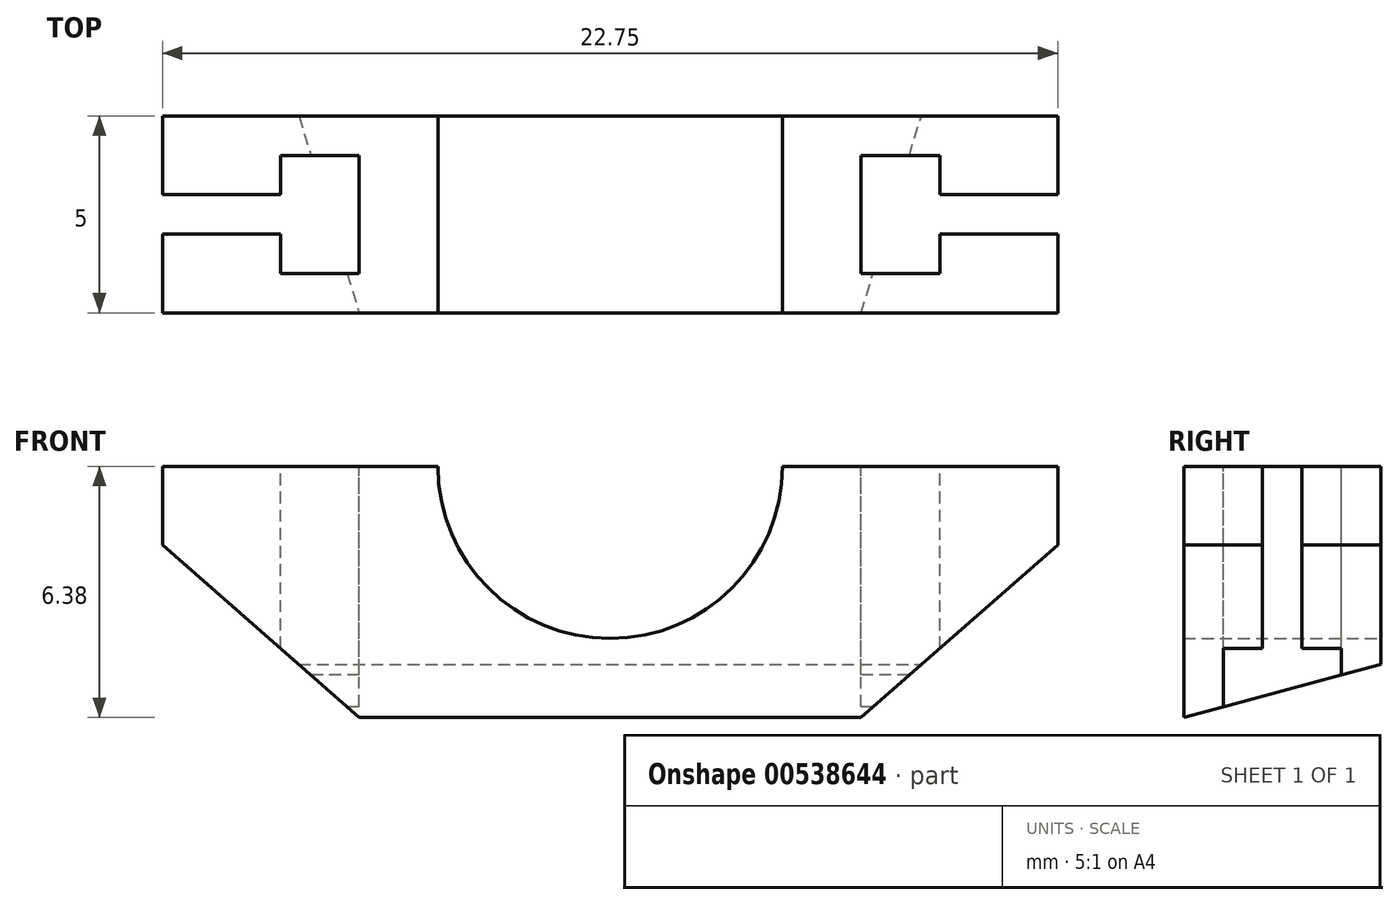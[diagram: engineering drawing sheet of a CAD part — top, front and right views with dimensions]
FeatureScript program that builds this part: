
annotation { "Feature Type Name" : "Feature", "Feature Type Description" : "" }
export const myFeature = defineFeature(function(context is Context, id is Id, definition is map)
    precondition{}
    {
        {
            var Q0;
            Q0=qCreatedBy(makeId("Front.planeOp"),FACE);
            var sketch = newSketch(context, id + "F0", { "sketchPlane" : qUnion([Q0])});
            skArc(sketch, "E0", {"start": v(-8.75, 0) * mm, "mid": v(-4.38, -4.38) * mm, "end": v(0, 0) * mm});
            skArc(sketch, "E1", {"start": v(-10.75, 0) * mm, "mid": v(-4.38, -6.38) * mm, "end": v(2, 0) * mm});
            skLineSegment(sketch, "E2", {"start": v(-10.75, 0) * mm, "end": v(-8.75, 0) * mm});
            skLineSegment(sketch, "E3", {"start": v(0, 0) * mm, "end": v(2, 0) * mm});
            skLineSegment(sketch, "E4.top", {"start": v(-10.75, -6.38) * mm, "end": v(2, -6.38) * mm});
            skLineSegment(sketch, "E4.left", {"start": v(-10.75, 0) * mm, "end": v(-10.75, -6.38) * mm});
            skLineSegment(sketch, "E4.right", {"start": v(2, 0) * mm, "end": v(2, -6.38) * mm});
            skLineSegment(sketch, "E5", {"start": v(2, 0) * mm, "end": v(7, 0) * mm});
            skLineSegment(sketch, "E6", {"start": v(7, 0) * mm, "end": v(7, -2) * mm});
            skLineSegment(sketch, "E7", {"start": v(7, -2) * mm, "end": v(2, -2) * mm});
            skLineSegment(sketch, "E8", {"start": v(-10.75, 0) * mm, "end": v(-15.75, 0) * mm});
            skLineSegment(sketch, "E9", {"start": v(-15.75, 0) * mm, "end": v(-15.75, -2) * mm});
            skLineSegment(sketch, "E10", {"start": v(-15.75, -2) * mm, "end": v(-10.75, -2) * mm});
            skSolve(sketch);
        }
        {
            var Q0;
            Q0 = qSketchRegion(id + "F0", true);
            extrude(context, id + "F1", {"entities" : qUnion([Q0]), "endBound" : BoundingType.SYMMETRIC, "depth" : 5 * mm, "offsetDistance" : 25 * mm});
        }
        {
            var Q0;
            Q0=makeQuery(id+"F1.opExtrude","SWEPT_FACE",FACE,{"disambiguationData":[OSD([sQuery(id+"F0.wireOp",EDGE,"E3"),sQuery(id+"F0.wireOp",EDGE,"E5")])]});
            var sketch = newSketch(context, id + "F2", { "sketchPlane" : qUnion([Q0])});
            skLineSegment(sketch, "E11.bottom", {"start": v(-15.75, 0.5) * mm, "end": v(-10.75, 0.5) * mm});
            skLineSegment(sketch, "E11.top", {"start": v(-15.75, -0.5) * mm, "end": v(-10.75, -0.5) * mm});
            skLineSegment(sketch, "E11.left", {"start": v(-15.75, 0.5) * mm, "end": v(-15.75, -0.5) * mm});
            skLineSegment(sketch, "E11.right", {"start": v(-10.75, 0.5) * mm, "end": v(-10.75, -0.5) * mm});
            skPoint(sketch, "E12", {"position": v(-15.75, 0) * mm});
            skLineSegment(sketch, "E13.bottom", {"start": v(-12.75, 1.5) * mm, "end": v(-10.75, 1.5) * mm});
            skLineSegment(sketch, "E13.top", {"start": v(-12.75, -1.5) * mm, "end": v(-10.75, -1.5) * mm});
            skLineSegment(sketch, "E13.left", {"start": v(-12.75, 1.5) * mm, "end": v(-12.75, -1.5) * mm});
            skLineSegment(sketch, "E13.right", {"start": v(-10.75, 1.5) * mm, "end": v(-10.75, -1.5) * mm});
            skPoint(sketch, "E13.middle", {"position": v(-11.75, 0) * mm});
            skLineSegment(sketch, "E14.MirrorCS", {"start": v(7, 0.5) * mm, "end": v(7, -0.5) * mm});
            skPoint(sketch, "E15.MirrorP", {"position": v(7, 0) * mm});
            skLineSegment(sketch, "E16.MirrorCS", {"start": v(2, 1.5) * mm, "end": v(2, -1.5) * mm});
            skLineSegment(sketch, "E17.MirrorCS", {"start": v(4, 1.5) * mm, "end": v(4, -1.5) * mm});
            skLineSegment(sketch, "E18.MirrorCS", {"start": v(4, -1.5) * mm, "end": v(2, -1.5) * mm});
            skPoint(sketch, "E19.MirrorP", {"position": v(3, 0) * mm});
            skLineSegment(sketch, "E20.MirrorCS", {"start": v(4, 1.5) * mm, "end": v(2, 1.5) * mm});
            skLineSegment(sketch, "E21.MirrorCS", {"start": v(2, 0.5) * mm, "end": v(2, -0.5) * mm});
            skLineSegment(sketch, "E22.MirrorCS", {"start": v(7, -0.5) * mm, "end": v(2, -0.5) * mm});
            skLineSegment(sketch, "E23.MirrorCS", {"start": v(7, 0.5) * mm, "end": v(2, 0.5) * mm});
            skSolve(sketch);
        }
        {
            var Q0;
            Q0 = qSketchRegion(id + "F2", true);
            extrude(context, id + "F3", {"entities" : qUnion([Q0]), "operationType" : NewBodyOperationType.REMOVE, "oppositeDirection" : true, "depth" : 25 * mm, "offsetDistance" : 25 * mm});
        }
        {
            var Q0;
            Q0=qCreatedBy(makeId("Top.planeOp"),FACE);
            var sketch = newSketch(context, id + "F4", { "sketchPlane" : qUnion([Q0])});
            skLineSegment(sketch, "E24", {"start": v(-15.75, 0) * mm, "end": v(7, 0) * mm, "construction": true});
            skLineSegment(sketch, "E25", {"start": v(-4.38, 2.7) * mm, "end": v(-4.38, -2.7) * mm, "construction": true});
            skPoint(sketch, "E25.startSnap0", {"position": v(-4.38, 0) * mm});
            skSolve(sketch);
        }
        {
            var Q0;
            Q0=makeQuery(id+"F3.boolean.opBoolean","MERGE",FACE,{"derivedFrom":[makeQuery(id+"F1.opExtrude","SWEPT_FACE",FACE,{"disambiguationData":[OSD([sQuery(id+"F0.wireOp",EDGE,"E4.right")])]}),makeQuery(id+"F3.opExtrude","SWEPT_FACE",FACE,{"disambiguationData":[OSD([sQuery(id+"F2.wireOp",EDGE,"E16.MirrorCS"),sQuery(id+"F2.wireOp",EDGE,"E21.MirrorCS")])]})]});
            var sketch = newSketch(context, id + "F5", { "sketchPlane" : qUnion([Q0])});
            skLineSegment(sketch, "E26", {"start": v(-2.5, -6.38) * mm, "end": v(2.5, -6.38) * mm});
            skLineSegment(sketch, "E27", {"start": v(-2.5, -6.38) * mm, "end": v(2.5, -5.04) * mm});
            skLineSegment(sketch, "E28", {"start": v(2.5, -6.38) * mm, "end": v(2.5, -5.04) * mm});
            skSolve(sketch);
        }
        {
            var Q0;
            Q0 = qSketchRegion(id + "F5", true);
            var Q1;
            Q1=makeQuery(id+"F5.imprint","IMPRINT",FACE,{"disambiguationData":[TD([[makeQuery(id+"F5.imprint","IMPRINT",EDGE,{"derivedFrom":sQuery(id+"F5.wireOp",EDGE,"E26")}),1.0]])]});
            extrude(context, id + "F6", {"entities" : qUnion([Q0, Q1]), "operationType" : NewBodyOperationType.REMOVE, "oppositeDirection" : true, "depth" : 25 * mm, "offsetDistance" : 25 * mm});
        }
        {
            var Q0;
            {var subQ0=sQuery(id+"F0.wireOp",EDGE,"E7");Q0=makeQuery(id+"Fhs1pQPk9hcDoOj_1.boolean.opBoolean","MERGE",FACE,{"derivedFrom":[makeQuery(id+"F1.opExtrude","CAP_FACE",FACE,{"disambiguationData":[OSD([sQuery(id+"F0.wireOp",EDGE,"E0"),sQuery(id+"F0.wireOp",EDGE,"E2"),sQuery(id+"F0.wireOp",EDGE,"E4.top"),sQuery(id+"F0.wireOp",EDGE,"E4.left"),sQuery(id+"F0.wireOp",EDGE,"E4.right"),sQuery(id+"F0.wireOp",EDGE,"E3"),sQuery(id+"F0.wireOp",EDGE,"E5"),sQuery(id+"F0.wireOp",EDGE,"E6"),subQ0,sQuery(id+"F0.wireOp",EDGE,"E8"),sQuery(id+"F0.wireOp",EDGE,"E9"),sQuery(id+"F0.wireOp",EDGE,"E10")])],"isStart":false}),makeQuery(id+"Fhs1pQPk9hcDoOj_1.opExtrude","SWEPT_FACE",FACE,{"disambiguationData":[OSD([subQ0]),TDD([makeQuery(id+"F1.opExtrude","CAP_EDGE",EDGE,{"disambiguationData":[OSD([subQ0])],"isStart":false})])]})]});}
            var sketch = newSketch(context, id + "F7", { "sketchPlane" : qUnion([Q0])});
            skLineSegment(sketch, "E29", {"start": v(-15.75, -2) * mm, "end": v(-10.75, -6.38) * mm});
            skLineSegment(sketch, "E30", {"start": v(2, -6.38) * mm, "end": v(7, -2) * mm});
            skSolve(sketch);
        }
        {
            var Q0;
            Q0 = qSketchRegion(id + "F7", true);
            var Q1;
            Q1=makeQuery(id+"F7.imprint","IMPRINT",FACE,{"disambiguationData":[TD([[makeQuery(id+"F7.imprint","IMPRINT",EDGE,{"derivedFrom":sQuery(id+"F7.wireOp",EDGE,"E29")}),1.0]])]});
            var Q2;
            Q2=makeQuery(id+"F7.imprint","IMPRINT",FACE,{"disambiguationData":[TD([[makeQuery(id+"F7.imprint","IMPRINT",EDGE,{"derivedFrom":sQuery(id+"F7.wireOp",EDGE,"E30")}),1.0]])]});
            var Q3;
            {var subQ0=sQuery(id+"F0.wireOp",EDGE,"E7");Q3=makeQuery(id+"Fhs1pQPk9hcDoOj_1.boolean.opBoolean","MERGE",FACE,{"derivedFrom":[makeQuery(id+"F1.opExtrude","CAP_FACE",FACE,{"disambiguationData":[OSD([sQuery(id+"F0.wireOp",EDGE,"E0"),sQuery(id+"F0.wireOp",EDGE,"E2"),sQuery(id+"F0.wireOp",EDGE,"E4.top"),sQuery(id+"F0.wireOp",EDGE,"E4.left"),sQuery(id+"F0.wireOp",EDGE,"E4.right"),sQuery(id+"F0.wireOp",EDGE,"E3"),sQuery(id+"F0.wireOp",EDGE,"E5"),sQuery(id+"F0.wireOp",EDGE,"E6"),subQ0,sQuery(id+"F0.wireOp",EDGE,"E8"),sQuery(id+"F0.wireOp",EDGE,"E9"),sQuery(id+"F0.wireOp",EDGE,"E10")])],"isStart":true}),makeQuery(id+"Fhs1pQPk9hcDoOj_1.opExtrude","SWEPT_FACE",FACE,{"disambiguationData":[OSD([subQ0]),TDD([makeQuery(id+"F1.opExtrude","CAP_EDGE",EDGE,{"disambiguationData":[OSD([subQ0])],"isStart":true})])]})]});}
            extrude(context, id + "F8", {"entities" : qUnion([Q0, Q1, Q2]), "operationType" : NewBodyOperationType.ADD, "endBound" : BoundingType.UP_TO_SURFACE, "oppositeDirection" : true, "depth" : 25 * mm, "endBoundEntityFace" : qUnion([Q3]), "offsetDistance" : 25 * mm});
        }
        {
            var Q0;
            Q0 = qSketchRegion(id + "F4", true);
            var Q1;
            Q1=makeQuery(id+"F5.imprint","IMPRINT",FACE,{"disambiguationData":[TD([[makeQuery(id+"F5.imprint","IMPRINT",EDGE,{"derivedFrom":sQuery(id+"F5.wireOp",EDGE,"E26")}),1.0]])]});
            extrude(context, id + "F9", {"entities" : qUnion([Q0, Q1]), "operationType" : NewBodyOperationType.REMOVE, "endBound" : BoundingType.SYMMETRIC, "oppositeDirection" : true, "depth" : 32.4 * mm, "offsetDistance" : 25 * mm});
        }
        {
            var Q0;
            Q0=makeQuery(id+"F8.opExtrude","SWEPT_FACE",FACE,{"disambiguationData":[OSD([sQuery(id+"F0.wireOp",EDGE,"E10")])]});
            var Q1;
            Q1=makeQuery(id+"F8.opExtrude","SWEPT_FACE",FACE,{"disambiguationData":[OSD([sQuery(id+"F0.wireOp",EDGE,"E7")])]});
            extrude(context, id + "F10", {"entities" : qUnion([Q0, Q1]), "operationType" : NewBodyOperationType.REMOVE, "oppositeDirection" : true, "depth" : 25 * mm, "offsetDistance" : 25 * mm});
        }
    });
